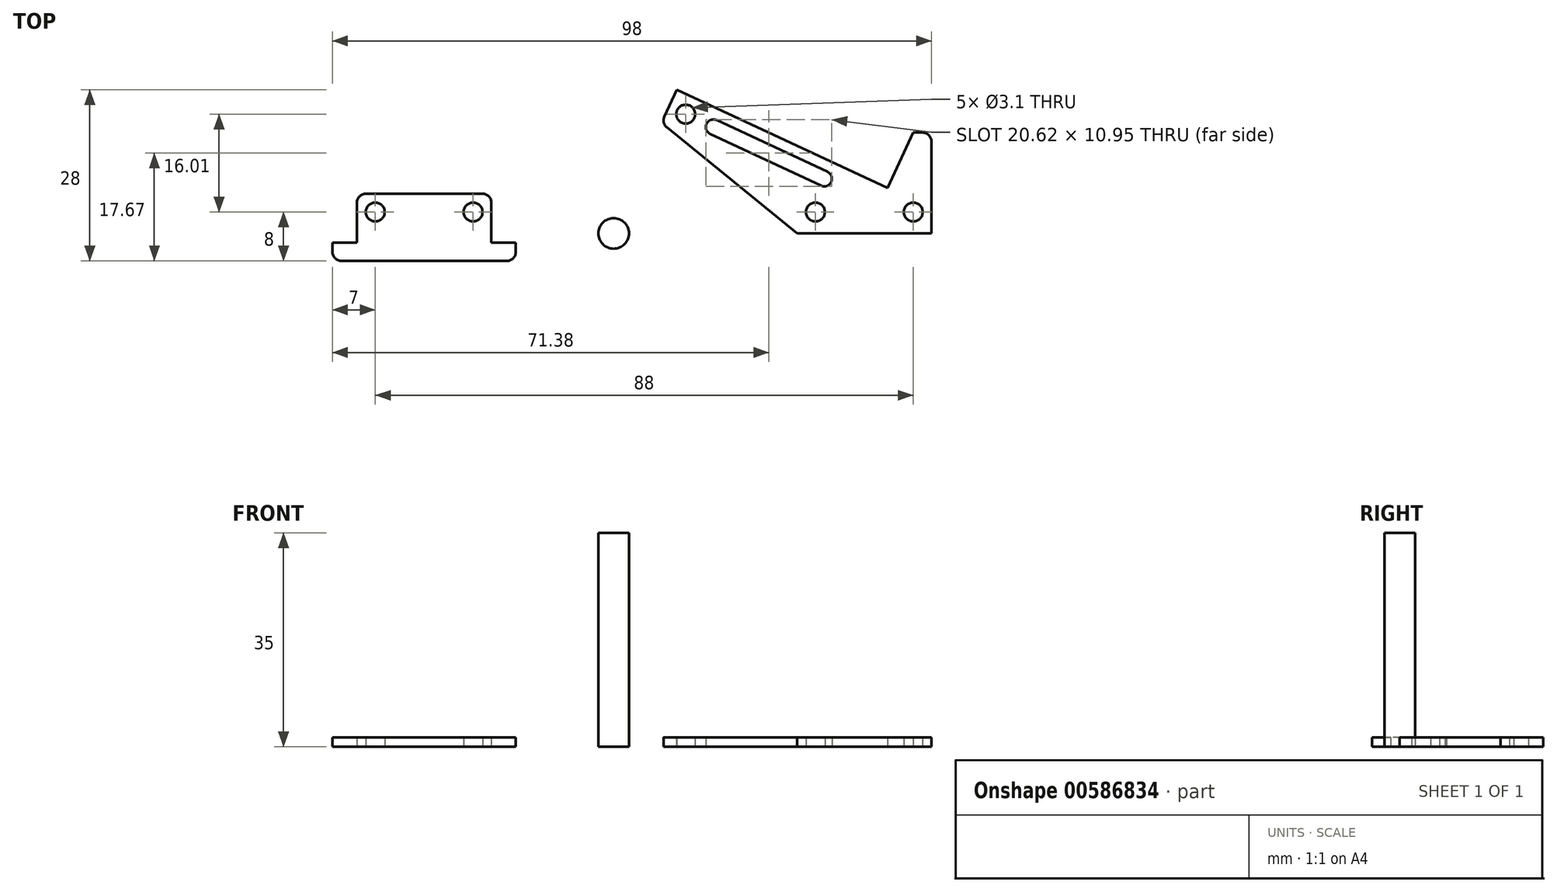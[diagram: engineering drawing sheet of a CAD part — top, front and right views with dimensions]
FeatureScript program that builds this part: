
annotation { "Feature Type Name" : "Feature", "Feature Type Description" : "" }
export const myFeature = defineFeature(function(context is Context, id is Id, definition is map)
    precondition{}
    {
        {
            var Q0;
            Q0=qCreatedBy(makeId("Top.planeOp"),FACE);
            var sketch = newSketch(context, id + "F0", { "sketchPlane" : qUnion([Q0])});
            skLineSegment(sketch, "E0", {"start": v(-42, 0) * mm, "end": v(-42, -1.5) * mm});
            skLineSegment(sketch, "E1", {"start": v(-42, -1.5) * mm, "end": v(-46, -1.5) * mm});
            skLineSegment(sketch, "E2", {"start": v(-46, -1.5) * mm, "end": v(-46, -3) * mm});
            skLineSegment(sketch, "E3", {"start": v(-44.5, -4.5) * mm, "end": v(-17.5, -4.5) * mm});
            skLineSegment(sketch, "E4", {"start": v(-16, -3) * mm, "end": v(-16, -1.5) * mm});
            skLineSegment(sketch, "E5", {"start": v(-16, -1.5) * mm, "end": v(-20, -1.5) * mm});
            skLineSegment(sketch, "E6", {"start": v(-20, -1.5) * mm, "end": v(-20, 0) * mm});
            skLineSegment(sketch, "E7", {"start": v(-42, 0) * mm, "end": v(-42, 5) * mm});
            skLineSegment(sketch, "E8", {"start": v(-40.5, 6.5) * mm, "end": v(-21.5, 6.5) * mm});
            skLineSegment(sketch, "E9", {"start": v(-20, 5) * mm, "end": v(-20, 0) * mm});
            skCircle(sketch, "E10", {"center": v(-39, 3.5) * mm, "radius": 1.55 * mm});
            skCircle(sketch, "E11", {"center": v(-23, 3.5) * mm, "radius": 1.55 * mm});
            skPoint(sketch, "E12.visualSharp", {"position": v(-46, -4.5) * mm});
            skArc(sketch, "E12.filletArc", {"start": v(-46, -3) * mm, "mid": v(-45.56, -4.06) * mm, "end": v(-44.5, -4.5) * mm});
            skPoint(sketch, "E13.visualSharp", {"position": v(-16, -4.5) * mm});
            skArc(sketch, "E13.filletArc", {"start": v(-17.5, -4.5) * mm, "mid": v(-16.44, -4.06) * mm, "end": v(-16, -3) * mm});
            skPoint(sketch, "E14.visualSharp", {"position": v(-42, 6.5) * mm});
            skArc(sketch, "E14.filletArc", {"start": v(-40.5, 6.5) * mm, "mid": v(-41.56, 6.06) * mm, "end": v(-42, 5) * mm});
            skPoint(sketch, "E15.visualSharp", {"position": v(-20, 6.5) * mm});
            skArc(sketch, "E15.filletArc", {"start": v(-20, 5) * mm, "mid": v(-20.44, 6.06) * mm, "end": v(-21.5, 6.5) * mm});
            skSolve(sketch);
        }
        {
            var Q0;
            Q0 = qSketchRegion(id + "F0", true);
            extrude(context, id + "F1", {"entities" : qUnion([Q0]), "depth" : 1.5 * mm, "offsetDistance" : 25 * mm});
        }
        {
            var Q0;
            Q0=qCreatedBy(makeId("Top.planeOp"),FACE);
            var sketch = newSketch(context, id + "F2", { "sketchPlane" : qUnion([Q0])});
            skLineSegment(sketch, "E16", {"start": v(10.33, 23.5) * mm, "end": v(44.77, 7.44) * mm});
            skLineSegment(sketch, "E17", {"start": v(44.77, 7.44) * mm, "end": v(49, 16.5) * mm});
            skLineSegment(sketch, "E18", {"start": v(49, 16.5) * mm, "end": v(50.5, 16.5) * mm});
            skLineSegment(sketch, "E19", {"start": v(52, 15) * mm, "end": v(52, 0) * mm});
            skLineSegment(sketch, "E20", {"start": v(52, 0) * mm, "end": v(30, 0) * mm});
            skLineSegment(sketch, "E21", {"start": v(8.3, 19.12) * mm, "end": v(10.33, 23.5) * mm});
            skPoint(sketch, "E22.visualSharp", {"position": v(52, 16.5) * mm});
            skArc(sketch, "E22.filletArc", {"start": v(52, 15) * mm, "mid": v(51.56, 16.06) * mm, "end": v(50.5, 16.5) * mm});
            skCircle(sketch, "E23", {"center": v(11.79, 19.5) * mm, "radius": 1.55 * mm});
            skCircle(sketch, "E24", {"center": v(33, 3.5) * mm, "radius": 1.55 * mm});
            skCircle(sketch, "E25", {"center": v(49, 3.5) * mm, "radius": 1.55 * mm});
            skLineSegment(sketch, "E26", {"start": v(16.85, 18.53) * mm, "end": v(34.97, 10.08) * mm});
            skLineSegment(sketch, "E27", {"start": v(15.79, 16.26) * mm, "end": v(33.91, 7.81) * mm});
            skLineSegment(sketch, "E28", {"start": v(15.79, 16.26) * mm, "end": v(16.85, 18.53) * mm, "construction": true});
            skLineSegment(sketch, "E29", {"start": v(33.91, 7.81) * mm, "end": v(34.97, 10.08) * mm, "construction": true});
            skArc(sketch, "E30", {"start": v(16.85, 18.53) * mm, "mid": v(15.18, 17.92) * mm, "end": v(15.79, 16.26) * mm});
            skArc(sketch, "E31", {"start": v(34.97, 10.08) * mm, "mid": v(35.58, 8.42) * mm, "end": v(33.91, 7.81) * mm});
            skLineSegment(sketch, "E32", {"start": v(8.7, 17.32) * mm, "end": v(30, 0) * mm});
            skPoint(sketch, "E33.visualSharp", {"position": v(7.8, 18.06) * mm});
            skArc(sketch, "E33.filletArc", {"start": v(8.3, 19.12) * mm, "mid": v(8.2, 18.15) * mm, "end": v(8.7, 17.32) * mm});
            skSolve(sketch);
        }
        {
            var Q0;
            Q0 = qSketchRegion(id + "F2", true);
            extrude(context, id + "F3", {"entities" : qUnion([Q0]), "depth" : 1.5 * mm, "offsetDistance" : 25 * mm});
        }
        {
            var Q0;
            Q0=qCreatedBy(makeId("Top.planeOp"),FACE);
            var sketch = newSketch(context, id + "F4", { "sketchPlane" : qUnion([Q0])});
            skCircle(sketch, "E34", {"center": v(0, 0) * mm, "radius": 2.5 * mm});
            skSolve(sketch);
        }
        {
            var Q0;
            Q0 = qSketchRegion(id + "F4", true);
            extrude(context, id + "F5", {"entities" : qUnion([Q0]), "depth" : 35 * mm, "offsetDistance" : 25 * mm});
        }
    });
